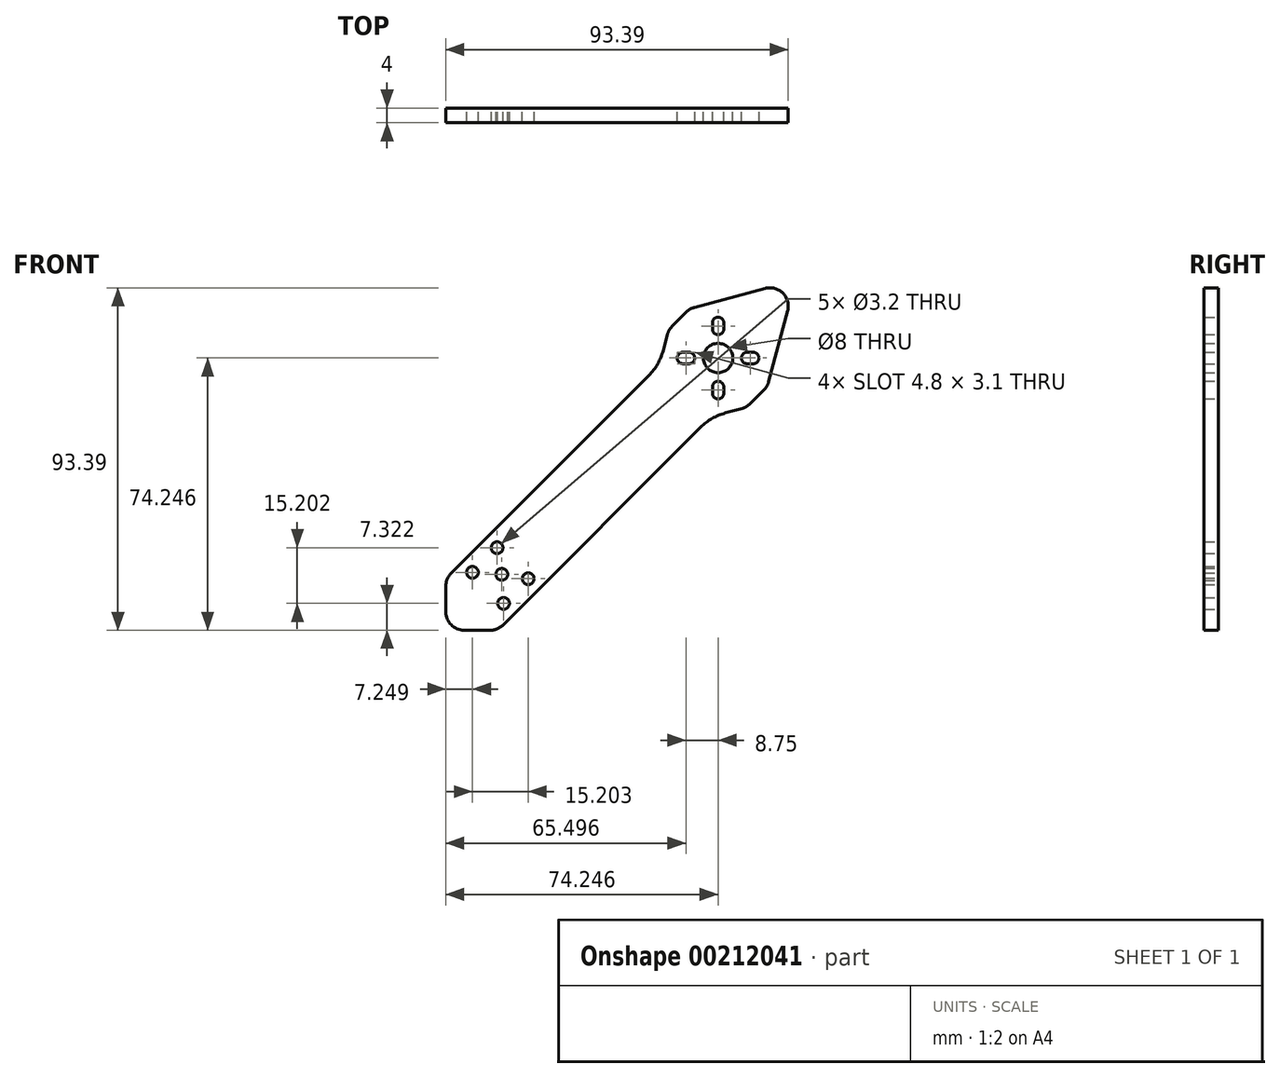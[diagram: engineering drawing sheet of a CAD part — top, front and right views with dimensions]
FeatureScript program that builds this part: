
annotation { "Feature Type Name" : "Feature", "Feature Type Description" : "" }
export const myFeature = defineFeature(function(context is Context, id is Id, definition is map)
    precondition{}
    {
        {
            var Q0;
            Q0=qCreatedBy(makeId("Front.planeOp"),FACE);
            var sketch = newSketch(context, id + "F0", { "sketchPlane" : qUnion([Q0])});
            skLineSegment(sketch, "E0", {"start": v(105.6, 105.6) * mm, "end": v(-91.93, -91.93) * mm, "construction": true});
            skLineSegment(sketch, "E1", {"start": v(53.41, 95.08) * mm, "end": v(99.76, 48.74) * mm, "construction": true});
            skPoint(sketch, "E2", {"position": v(0, 0) * mm});
            skCircle(sketch, "E3", {"center": v(74.25, 74.25) * mm, "radius": 4 * mm});
            skLineSegment(sketch, "E4", {"start": v(1.46, 15.6) * mm, "end": v(55.37, 69.5) * mm});
            skLineSegment(sketch, "E5", {"start": v(15.6, 1.46) * mm, "end": v(69.5, 55.37) * mm});
            skLineSegment(sketch, "E6", {"start": v(74.25, 40.06) * mm, "end": v(74.25, 102.92) * mm, "construction": true});
            skLineSegment(sketch, "E7", {"start": v(134.55, 74.25) * mm, "end": v(21.47, 74.25) * mm, "construction": true});
            skArc(sketch, "E8", {"start": v(75.8, 83.85) * mm, "mid": v(74.25, 85.4) * mm, "end": v(72.7, 83.85) * mm});
            skArc(sketch, "E9", {"start": v(72.7, 82.15) * mm, "mid": v(74.25, 80.6) * mm, "end": v(75.8, 82.15) * mm});
            skLineSegment(sketch, "E10", {"start": v(72.7, 83.85) * mm, "end": v(72.7, 82.15) * mm});
            skLineSegment(sketch, "E11.MirrorCS", {"start": v(75.8, 83.85) * mm, "end": v(75.8, 82.15) * mm});
            skArc(sketch, "E12.1.0", {"start": v(64.65, 75.8) * mm, "mid": v(63.1, 74.25) * mm, "end": v(64.65, 72.7) * mm});
            skLineSegment(sketch, "E12.1.1", {"start": v(64.65, 72.7) * mm, "end": v(66.35, 72.7) * mm});
            skLineSegment(sketch, "E12.1.2", {"start": v(64.65, 75.8) * mm, "end": v(66.35, 75.8) * mm});
            skArc(sketch, "E12.1.3", {"start": v(66.35, 72.7) * mm, "mid": v(67.9, 74.25) * mm, "end": v(66.35, 75.8) * mm});
            skArc(sketch, "E12.2.0", {"start": v(72.7, 64.65) * mm, "mid": v(74.25, 63.1) * mm, "end": v(75.8, 64.65) * mm});
            skLineSegment(sketch, "E12.2.1", {"start": v(75.8, 64.65) * mm, "end": v(75.8, 66.35) * mm});
            skLineSegment(sketch, "E12.2.2", {"start": v(72.7, 64.65) * mm, "end": v(72.7, 66.35) * mm});
            skArc(sketch, "E12.2.3", {"start": v(75.8, 66.35) * mm, "mid": v(74.25, 67.9) * mm, "end": v(72.7, 66.35) * mm});
            skArc(sketch, "E12.3.0", {"start": v(83.85, 72.7) * mm, "mid": v(85.4, 74.25) * mm, "end": v(83.85, 75.8) * mm});
            skLineSegment(sketch, "E12.3.1", {"start": v(83.85, 75.8) * mm, "end": v(82.15, 75.8) * mm});
            skLineSegment(sketch, "E12.3.2", {"start": v(83.85, 72.7) * mm, "end": v(82.15, 72.7) * mm});
            skArc(sketch, "E12.3.3", {"start": v(82.15, 75.8) * mm, "mid": v(80.6, 74.25) * mm, "end": v(82.15, 72.7) * mm});
            skLineSegment(sketch, "E13", {"start": v(61.74, 82.96) * mm, "end": v(65.53, 86.75) * mm});
            skLineSegment(sketch, "E14", {"start": v(82.96, 61.74) * mm, "end": v(86.75, 65.53) * mm});
            skPoint(sketch, "E15", {"position": v(95.46, 95.46) * mm});
            skLineSegment(sketch, "E16", {"start": v(67.78, 88.04) * mm, "end": v(87.1, 93.22) * mm});
            skLineSegment(sketch, "E17", {"start": v(88.04, 67.78) * mm, "end": v(93.22, 87.1) * mm});
            skLineSegment(sketch, "E18", {"start": v(57.97, 96.2) * mm, "end": v(99.95, 54.23) * mm, "construction": true});
            skArc(sketch, "E19.filletArc", {"start": v(93.22, 87.1) * mm, "mid": v(91.92, 91.92) * mm, "end": v(87.1, 93.22) * mm});
            skLineSegment(sketch, "E20", {"start": v(59.25, 76.23) * mm, "end": v(60.45, 80.72) * mm});
            skLineSegment(sketch, "E21", {"start": v(76.23, 59.25) * mm, "end": v(80.72, 60.45) * mm});
            skPoint(sketch, "E22.visualSharp", {"position": v(58.2, 72.35) * mm});
            skArc(sketch, "E22.filletArc", {"start": v(55.37, 69.5) * mm, "mid": v(57.75, 72.62) * mm, "end": v(59.25, 76.23) * mm});
            skPoint(sketch, "E23.visualSharp", {"position": v(72.35, 58.2) * mm});
            skArc(sketch, "E23.filletArc", {"start": v(76.23, 59.25) * mm, "mid": v(72.62, 57.75) * mm, "end": v(69.5, 55.37) * mm});
            skPoint(sketch, "E24.visualSharp", {"position": v(60.8, 82.01) * mm});
            skArc(sketch, "E24.filletArc", {"start": v(61.74, 82.96) * mm, "mid": v(60.95, 81.92) * mm, "end": v(60.45, 80.72) * mm});
            skPoint(sketch, "E25.visualSharp", {"position": v(66.48, 87.7) * mm});
            skArc(sketch, "E25.filletArc", {"start": v(67.78, 88.04) * mm, "mid": v(66.57, 87.54) * mm, "end": v(65.53, 86.75) * mm});
            skPoint(sketch, "E26.visualSharp", {"position": v(82.01, 60.8) * mm});
            skArc(sketch, "E26.filletArc", {"start": v(80.72, 60.45) * mm, "mid": v(81.92, 60.95) * mm, "end": v(82.96, 61.74) * mm});
            skPoint(sketch, "E27.visualSharp", {"position": v(87.7, 66.48) * mm});
            skArc(sketch, "E27.filletArc", {"start": v(86.75, 65.53) * mm, "mid": v(87.54, 66.57) * mm, "end": v(88.04, 67.78) * mm});
            skLineSegment(sketch, "E28", {"start": v(0, 12.07) * mm, "end": v(0, 5) * mm});
            skLineSegment(sketch, "E29", {"start": v(12.07, 0) * mm, "end": v(5, 0) * mm});
            skPoint(sketch, "E30.visualSharp", {"position": v(0, 14.14) * mm});
            skArc(sketch, "E30.filletArc", {"start": v(1.46, 15.6) * mm, "mid": v(0.38, 13.98) * mm, "end": v(0, 12.07) * mm});
            skPoint(sketch, "E31.visualSharp", {"position": v(14.14, 0) * mm});
            skArc(sketch, "E31.filletArc", {"start": v(12.07, 0) * mm, "mid": v(13.98, 0.38) * mm, "end": v(15.6, 1.46) * mm});
            skArc(sketch, "E32.filletArc", {"start": v(0, 5) * mm, "mid": v(1.46, 1.46) * mm, "end": v(5, 0) * mm});
            skCircle(sketch, "E33", {"center": v(15.73, 7.32) * mm, "radius": 1.6 * mm});
            skCircle(sketch, "E34", {"center": v(13.97, 22.52) * mm, "radius": 1.6 * mm});
            skCircle(sketch, "E35", {"center": v(7.25, 15.8) * mm, "radius": 1.6 * mm});
            skCircle(sketch, "E36", {"center": v(22.45, 14.04) * mm, "radius": 1.6 * mm});
            skCircle(sketch, "E37", {"center": v(15.25, 15.25) * mm, "radius": 1.6 * mm});
            skSolve(sketch);
        }
        {
            var Q0;
            Q0 = qSketchRegion(id + "F0", true);
            extrude(context, id + "F1", {"entities" : qUnion([Q0]), "depth" : 4 * mm});
        }
    });
